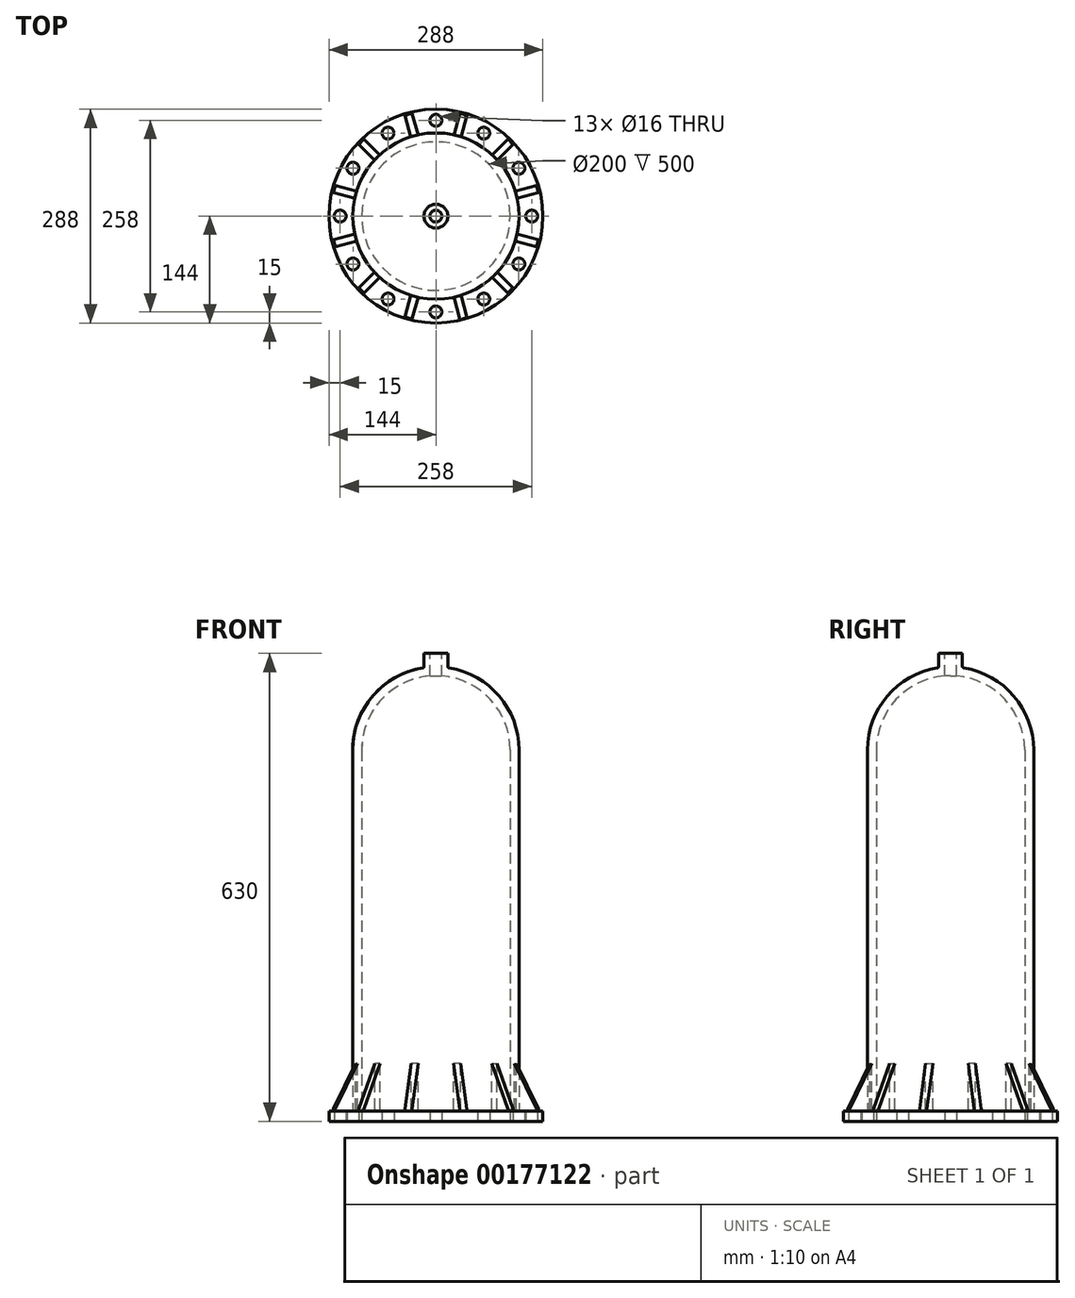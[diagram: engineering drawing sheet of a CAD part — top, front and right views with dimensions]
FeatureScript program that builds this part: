
annotation { "Feature Type Name" : "Feature", "Feature Type Description" : "" }
export const myFeature = defineFeature(function(context is Context, id is Id, definition is map)
    precondition{}
    {
        {
            var Q0;
            Q0=qCreatedBy(makeId("Front.planeOp"),FACE);
            var sketch = newSketch(context, id + "F0", { "sketchPlane" : qUnion([Q0])});
            skLineSegment(sketch, "E0", {"start": v(-144, 0) * mm, "end": v(-100, 0) * mm});
            skLineSegment(sketch, "E1", {"start": v(-100, 0) * mm, "end": v(-100, 500) * mm});
            skLineSegment(sketch, "E2", {"start": v(-144, 0) * mm, "end": v(-144, 14) * mm});
            skLineSegment(sketch, "E3", {"start": v(-16, 610.85) * mm, "end": v(-16, 630) * mm});
            skLineSegment(sketch, "E4", {"start": v(-16, 630) * mm, "end": v(0, 630) * mm});
            skLineSegment(sketch, "E5", {"start": v(0, 630) * mm, "end": v(0, 600) * mm});
            skLineSegment(sketch, "E6", {"start": v(0, 0) * mm, "end": v(0, 600) * mm, "construction": true});
            skPoint(sketch, "E7", {"position": v(0, 615) * mm});
            skLineSegment(sketch, "E8", {"start": v(-144, 14) * mm, "end": v(-112, 14) * mm});
            skLineSegment(sketch, "E9", {"start": v(-112, 14) * mm, "end": v(-112, 500) * mm});
            skArc(sketch, "E10", {"start": v(0, 600) * mm, "mid": v(-70.71, 570.71) * mm, "end": v(-100, 500) * mm});
            skArc(sketch, "E11", {"start": v(-16, 610.85) * mm, "mid": v(-84.66, 573.32) * mm, "end": v(-112, 500) * mm});
            skLineSegment(sketch, "E12", {"start": v(-112, 500) * mm, "end": v(0, 500) * mm, "construction": true});
            skSolve(sketch);
        }
        {
            var Q0;
            Q0 = qSketchRegion(id + "F0", true);
            var Q1;
            Q1=sQuery(id+"F0.wireOp",EDGE,"E6");
            revolve(context, id + "F1", {"entities" : qUnion([Q0]), "axis" : qUnion([Q1]), "revolveType" : RevolveType.FULL});
        }
        {
            var Q0;
            Q0=makeQuery(id+"F1.opRevolve","SWEPT_FACE",FACE,{"disambiguationData":[OSD([sQuery(id+"F0.wireOp",EDGE,"E0")])]});
            var sketch = newSketch(context, id + "F2", { "sketchPlane" : qUnion([Q0])});
            skCircle(sketch, "E13", {"center": v(0, -129) * mm, "radius": 8 * mm});
            skSolve(sketch);
        }
        {
            var Q0;
            Q0=makeQuery(id+"F2.imprint","IMPRINT",FACE,{"disambiguationData":[TD([[makeQuery(id+"F2.imprint","IMPRINT",EDGE,{"derivedFrom":sQuery(id+"F2.wireOp",EDGE,"E13")}),1.0]])]});
            extrude(context, id + "F3", {"entities" : qUnion([Q0]), "oppositeDirection" : true, "depth" : 20 * mm});
        }
        {
            var Q0;
            Q0=makeQuery(id+"F3.opExtrude","SWEPT_BODY",BODY,{"disambiguationData":[OSD([sQuery(id+"F2.wireOp",EDGE,"E13")])]});
            var Q1;
            Q1=makeQuery(id+"F1.opRevolve","SWEPT_EDGE",EDGE,{"disambiguationData":[OSD([sQuery(id+"F0.wireOp",EDGE,"E0"),sQuery(id+"F0.wireOp",EDGE,"E2")])]});
            circularPattern(context, id + "F4", {"entities" : qUnion([Q0]), "axis" : qUnion([Q1]), "angle" : 30 * degree, "instanceCount" : 12});
        }
        {
            var Q0;
            Q0=makeQuery(id+"F3.opExtrude","SWEPT_BODY",BODY,{"disambiguationData":[OSD([sQuery(id+"F2.wireOp",EDGE,"E13")])]});
            var Q1;
            Q1=makeQuery(id+"F4.opPattern","COPY",BODY,{"derivedFrom":makeQuery(id+"F3.opExtrude","SWEPT_BODY",BODY,{"disambiguationData":[OSD([sQuery(id+"F2.wireOp",EDGE,"E13")])]}),"instanceName":"2"});
            var Q2;
            Q2=makeQuery(id+"F4.opPattern","COPY",BODY,{"derivedFrom":makeQuery(id+"F3.opExtrude","SWEPT_BODY",BODY,{"disambiguationData":[OSD([sQuery(id+"F2.wireOp",EDGE,"E13")])]}),"instanceName":"4"});
            var Q3;
            Q3=makeQuery(id+"F4.opPattern","COPY",BODY,{"derivedFrom":makeQuery(id+"F3.opExtrude","SWEPT_BODY",BODY,{"disambiguationData":[OSD([sQuery(id+"F2.wireOp",EDGE,"E13")])]}),"instanceName":"6"});
            var Q4;
            Q4=makeQuery(id+"F4.opPattern","COPY",BODY,{"derivedFrom":makeQuery(id+"F3.opExtrude","SWEPT_BODY",BODY,{"disambiguationData":[OSD([sQuery(id+"F2.wireOp",EDGE,"E13")])]}),"instanceName":"8"});
            var Q5;
            Q5=makeQuery(id+"F4.opPattern","COPY",BODY,{"derivedFrom":makeQuery(id+"F3.opExtrude","SWEPT_BODY",BODY,{"disambiguationData":[OSD([sQuery(id+"F2.wireOp",EDGE,"E13")])]}),"instanceName":"11"});
            var Q6;
            Q6=makeQuery(id+"F4.opPattern","COPY",BODY,{"derivedFrom":makeQuery(id+"F3.opExtrude","SWEPT_BODY",BODY,{"disambiguationData":[OSD([sQuery(id+"F2.wireOp",EDGE,"E13")])]}),"instanceName":"10"});
            var Q7;
            Q7=makeQuery(id+"F4.opPattern","COPY",BODY,{"derivedFrom":makeQuery(id+"F3.opExtrude","SWEPT_BODY",BODY,{"disambiguationData":[OSD([sQuery(id+"F2.wireOp",EDGE,"E13")])]}),"instanceName":"9"});
            var Q8;
            Q8=makeQuery(id+"F4.opPattern","COPY",BODY,{"derivedFrom":makeQuery(id+"F3.opExtrude","SWEPT_BODY",BODY,{"disambiguationData":[OSD([sQuery(id+"F2.wireOp",EDGE,"E13")])]}),"instanceName":"7"});
            var Q9;
            Q9=makeQuery(id+"F4.opPattern","COPY",BODY,{"derivedFrom":makeQuery(id+"F3.opExtrude","SWEPT_BODY",BODY,{"disambiguationData":[OSD([sQuery(id+"F2.wireOp",EDGE,"E13")])]}),"instanceName":"5"});
            var Q10;
            Q10=makeQuery(id+"F4.opPattern","COPY",BODY,{"derivedFrom":makeQuery(id+"F3.opExtrude","SWEPT_BODY",BODY,{"disambiguationData":[OSD([sQuery(id+"F2.wireOp",EDGE,"E13")])]}),"instanceName":"3"});
            var Q11;
            Q11=makeQuery(id+"F4.opPattern","COPY",BODY,{"derivedFrom":makeQuery(id+"F3.opExtrude","SWEPT_BODY",BODY,{"disambiguationData":[OSD([sQuery(id+"F2.wireOp",EDGE,"E13")])]}),"instanceName":"1"});
            var Q12;
            Q12=makeQuery(id+"F1.opRevolve","SWEPT_BODY",BODY,{"disambiguationData":[OSD([sQuery(id+"F0.wireOp",EDGE,"E0"),sQuery(id+"F0.wireOp",EDGE,"E1"),sQuery(id+"F0.wireOp",EDGE,"E2"),sQuery(id+"F0.wireOp",EDGE,"E3"),sQuery(id+"F0.wireOp",EDGE,"E4"),sQuery(id+"F0.wireOp",EDGE,"E5"),sQuery(id+"F0.wireOp",EDGE,"E8"),sQuery(id+"F0.wireOp",EDGE,"E9"),sQuery(id+"F0.wireOp",EDGE,"E10"),sQuery(id+"F0.wireOp",EDGE,"E11")])]});
            booleanBodies(context, id + "F5", {"operationType" : BooleanOperationType.SUBTRACTION, "tools" : qUnion([Q0, Q1, Q2, Q3, Q4, Q5, Q6, Q7, Q8, Q9, Q10, Q11]), "targets" : qUnion([Q12])});
        }
        {
            var Q0;
            Q0=sQuery(id+"F0.wireOp",EDGE,"E6");
            cPlane(context, id + "F6", {"entities" : qUnion([Q0]), "cplaneType" : CPlaneType.LINE_ANGLE, "offset" : 25 * mm, "angle" : 45 * degree, "width" : 150 * mm, "height" : 150 * mm});
        }
        {
            var Q0;
            Q0=qCreatedBy(id+"F6.planeOp",FACE);
            var sketch = newSketch(context, id + "F7", { "sketchPlane" : qUnion([Q0])});
            skLineSegment(sketch, "E14", {"start": v(-111, 78) * mm, "end": v(-143, 14) * mm});
            skLineSegment(sketch, "E15", {"start": v(-143, 14) * mm, "end": v(-111, 14) * mm});
            skLineSegment(sketch, "E16", {"start": v(-111, 14) * mm, "end": v(-111, 78) * mm});
            skSolve(sketch);
        }
        {
            var Q0;
            Q0=makeQuery(id+"F7.imprint","IMPRINT",FACE,{"disambiguationData":[TD([[makeQuery(id+"F7.imprint","IMPRINT",EDGE,{"derivedFrom":sQuery(id+"F7.wireOp",EDGE,"E14")}),1.0]])]});
            extrude(context, id + "F8", {"entities" : qUnion([Q0]), "endBound" : BoundingType.SYMMETRIC, "depth" : 10 * mm});
        }
        {
            var Q0;
            Q0=makeQuery(id+"F8.opExtrude","SWEPT_BODY",BODY,{"disambiguationData":[OSD([sQuery(id+"F7.wireOp",EDGE,"E14"),sQuery(id+"F7.wireOp",EDGE,"E15"),sQuery(id+"F7.wireOp",EDGE,"E16")])]});
            var Q1;
            Q1=makeQuery(id+"F1.opRevolve","SWEPT_EDGE",EDGE,{"disambiguationData":[OSD([sQuery(id+"F0.wireOp",EDGE,"E0"),sQuery(id+"F0.wireOp",EDGE,"E2")])]});
            circularPattern(context, id + "F9", {"entities" : qUnion([Q0]), "axis" : qUnion([Q1]), "angle" : 30 * degree, "instanceCount" : 12});
        }
        {
            var Q0;
            Q0=makeQuery(id+"F1.opRevolve","SWEPT_FACE",FACE,{"disambiguationData":[OSD([sQuery(id+"F0.wireOp",EDGE,"E4")])]});
            var sketch = newSketch(context, id + "F10", { "sketchPlane" : qUnion([Q0])});
            skCircle(sketch, "E17", {"center": v(0, 0) * mm, "radius": 8 * mm});
            skSolve(sketch);
        }
        {
            var Q0;
            Q0=makeQuery(id+"F10.imprint","IMPRINT",FACE,{"disambiguationData":[TD([[makeQuery(id+"F10.imprint","IMPRINT",EDGE,{"derivedFrom":sQuery(id+"F10.wireOp",EDGE,"E17")}),1.0]])]});
            extrude(context, id + "F11", {"entities" : qUnion([Q0]), "operationType" : NewBodyOperationType.REMOVE, "endBound" : BoundingType.THROUGH_ALL, "oppositeDirection" : true, "depth" : 25 * mm});
        }
        {
            var Q0;
            Q0=makeQuery(id+"F1.opRevolve","SWEPT_EDGE",EDGE,{"disambiguationData":[OSD([sQuery(id+"F0.wireOp",EDGE,"E3"),sQuery(id+"F0.wireOp",EDGE,"E11")])]});
            fillet(context, id + "F12", {"entities" : qUnion([Q0]), "radius" : 2 * mm, "tangentPropagation" : true, "allowEdgeOverflow" : false});
        }
        {
            var Q0;
            Q0=makeQuery(id+"F1.opRevolve","SWEPT_FACE",FACE,{"disambiguationData":[OSD([sQuery(id+"F0.wireOp",EDGE,"E9")])]});
            fillet(context, id + "F13", {"entities" : qUnion([Q0]), "radius" : 2 * mm, "tangentPropagation" : true, "allowEdgeOverflow" : false});
        }
        {
            var Q0;
            Q0=makeQuery(id+"F9.opPattern","COPY",EDGE,{"derivedFrom":makeQuery(id+"F8.opExtrude","CAP_EDGE",EDGE,{"disambiguationData":[OSD([sQuery(id+"F7.wireOp",EDGE,"E15")])],"isStart":true}),"instanceName":"2"});
            var Q1;
            Q1=makeQuery(id+"F9.opPattern","COPY",EDGE,{"derivedFrom":makeQuery(id+"F8.opExtrude","CAP_EDGE",EDGE,{"disambiguationData":[OSD([sQuery(id+"F7.wireOp",EDGE,"E15")])],"isStart":false}),"instanceName":"2"});
            var Q2;
            Q2=makeQuery(id+"F9.opPattern","COPY",EDGE,{"derivedFrom":makeQuery(id+"F8.opExtrude","CAP_EDGE",EDGE,{"disambiguationData":[OSD([sQuery(id+"F7.wireOp",EDGE,"E15")])],"isStart":false}),"instanceName":"3"});
            var Q3;
            Q3=makeQuery(id+"F9.opPattern","COPY",EDGE,{"derivedFrom":makeQuery(id+"F8.opExtrude","SWEPT_EDGE",EDGE,{"disambiguationData":[OSD([sQuery(id+"F7.wireOp",EDGE,"E14"),sQuery(id+"F7.wireOp",EDGE,"E15")])]}),"instanceName":"2"});
            var Q4;
            Q4=makeQuery(id+"F9.opPattern","COPY",EDGE,{"derivedFrom":makeQuery(id+"F8.opExtrude","SWEPT_EDGE",EDGE,{"disambiguationData":[OSD([sQuery(id+"F7.wireOp",EDGE,"E14"),sQuery(id+"F7.wireOp",EDGE,"E15")])]}),"instanceName":"3"});
            var Q5;
            Q5=makeQuery(id+"F9.opPattern","COPY",EDGE,{"derivedFrom":makeQuery(id+"F8.opExtrude","CAP_EDGE",EDGE,{"disambiguationData":[OSD([sQuery(id+"F7.wireOp",EDGE,"E15")])],"isStart":true}),"instanceName":"3"});
            var Q6;
            Q6=makeQuery(id+"F9.opPattern","COPY",EDGE,{"derivedFrom":makeQuery(id+"F8.opExtrude","CAP_EDGE",EDGE,{"disambiguationData":[OSD([sQuery(id+"F7.wireOp",EDGE,"E15")])],"isStart":false}),"instanceName":"4"});
            var Q7;
            Q7=makeQuery(id+"F9.opPattern","COPY",EDGE,{"derivedFrom":makeQuery(id+"F8.opExtrude","SWEPT_EDGE",EDGE,{"disambiguationData":[OSD([sQuery(id+"F7.wireOp",EDGE,"E14"),sQuery(id+"F7.wireOp",EDGE,"E15")])]}),"instanceName":"4"});
            var Q8;
            Q8=makeQuery(id+"F9.opPattern","COPY",EDGE,{"derivedFrom":makeQuery(id+"F8.opExtrude","CAP_EDGE",EDGE,{"disambiguationData":[OSD([sQuery(id+"F7.wireOp",EDGE,"E15")])],"isStart":true}),"instanceName":"4"});
            var Q9;
            Q9=makeQuery(id+"F9.opPattern","COPY",EDGE,{"derivedFrom":makeQuery(id+"F8.opExtrude","CAP_EDGE",EDGE,{"disambiguationData":[OSD([sQuery(id+"F7.wireOp",EDGE,"E15")])],"isStart":false}),"instanceName":"5"});
            var Q10;
            Q10=makeQuery(id+"F9.opPattern","COPY",EDGE,{"derivedFrom":makeQuery(id+"F8.opExtrude","SWEPT_EDGE",EDGE,{"disambiguationData":[OSD([sQuery(id+"F7.wireOp",EDGE,"E14"),sQuery(id+"F7.wireOp",EDGE,"E15")])]}),"instanceName":"5"});
            var Q11;
            Q11=makeQuery(id+"F9.opPattern","COPY",EDGE,{"derivedFrom":makeQuery(id+"F8.opExtrude","CAP_EDGE",EDGE,{"disambiguationData":[OSD([sQuery(id+"F7.wireOp",EDGE,"E15")])],"isStart":true}),"instanceName":"5"});
            var Q12;
            Q12=makeQuery(id+"F9.opPattern","COPY",EDGE,{"derivedFrom":makeQuery(id+"F8.opExtrude","CAP_EDGE",EDGE,{"disambiguationData":[OSD([sQuery(id+"F7.wireOp",EDGE,"E15")])],"isStart":false}),"instanceName":"6"});
            var Q13;
            Q13=makeQuery(id+"F9.opPattern","COPY",EDGE,{"derivedFrom":makeQuery(id+"F8.opExtrude","SWEPT_EDGE",EDGE,{"disambiguationData":[OSD([sQuery(id+"F7.wireOp",EDGE,"E14"),sQuery(id+"F7.wireOp",EDGE,"E15")])]}),"instanceName":"6"});
            var Q14;
            Q14=makeQuery(id+"F9.opPattern","COPY",EDGE,{"derivedFrom":makeQuery(id+"F8.opExtrude","CAP_EDGE",EDGE,{"disambiguationData":[OSD([sQuery(id+"F7.wireOp",EDGE,"E15")])],"isStart":true}),"instanceName":"6"});
            var Q15;
            Q15=makeQuery(id+"F9.opPattern","COPY",EDGE,{"derivedFrom":makeQuery(id+"F8.opExtrude","CAP_EDGE",EDGE,{"disambiguationData":[OSD([sQuery(id+"F7.wireOp",EDGE,"E15")])],"isStart":false}),"instanceName":"7"});
            var Q16;
            Q16=makeQuery(id+"F9.opPattern","COPY",EDGE,{"derivedFrom":makeQuery(id+"F8.opExtrude","SWEPT_EDGE",EDGE,{"disambiguationData":[OSD([sQuery(id+"F7.wireOp",EDGE,"E14"),sQuery(id+"F7.wireOp",EDGE,"E15")])]}),"instanceName":"7"});
            var Q17;
            Q17=makeQuery(id+"F9.opPattern","COPY",EDGE,{"derivedFrom":makeQuery(id+"F8.opExtrude","CAP_EDGE",EDGE,{"disambiguationData":[OSD([sQuery(id+"F7.wireOp",EDGE,"E15")])],"isStart":true}),"instanceName":"7"});
            var Q18;
            Q18=makeQuery(id+"F9.opPattern","COPY",EDGE,{"derivedFrom":makeQuery(id+"F8.opExtrude","CAP_EDGE",EDGE,{"disambiguationData":[OSD([sQuery(id+"F7.wireOp",EDGE,"E15")])],"isStart":false}),"instanceName":"8"});
            var Q19;
            Q19=makeQuery(id+"F9.opPattern","COPY",EDGE,{"derivedFrom":makeQuery(id+"F8.opExtrude","SWEPT_EDGE",EDGE,{"disambiguationData":[OSD([sQuery(id+"F7.wireOp",EDGE,"E14"),sQuery(id+"F7.wireOp",EDGE,"E15")])]}),"instanceName":"8"});
            var Q20;
            Q20=makeQuery(id+"F9.opPattern","COPY",EDGE,{"derivedFrom":makeQuery(id+"F8.opExtrude","CAP_EDGE",EDGE,{"disambiguationData":[OSD([sQuery(id+"F7.wireOp",EDGE,"E15")])],"isStart":true}),"instanceName":"8"});
            var Q21;
            Q21=makeQuery(id+"F9.opPattern","COPY",EDGE,{"derivedFrom":makeQuery(id+"F8.opExtrude","CAP_EDGE",EDGE,{"disambiguationData":[OSD([sQuery(id+"F7.wireOp",EDGE,"E15")])],"isStart":false}),"instanceName":"9"});
            var Q22;
            Q22=makeQuery(id+"F9.opPattern","COPY",EDGE,{"derivedFrom":makeQuery(id+"F8.opExtrude","SWEPT_EDGE",EDGE,{"disambiguationData":[OSD([sQuery(id+"F7.wireOp",EDGE,"E14"),sQuery(id+"F7.wireOp",EDGE,"E15")])]}),"instanceName":"9"});
            var Q23;
            Q23=makeQuery(id+"F9.opPattern","COPY",EDGE,{"derivedFrom":makeQuery(id+"F8.opExtrude","CAP_EDGE",EDGE,{"disambiguationData":[OSD([sQuery(id+"F7.wireOp",EDGE,"E15")])],"isStart":true}),"instanceName":"9"});
            var Q24;
            Q24=makeQuery(id+"F9.opPattern","COPY",EDGE,{"derivedFrom":makeQuery(id+"F8.opExtrude","CAP_EDGE",EDGE,{"disambiguationData":[OSD([sQuery(id+"F7.wireOp",EDGE,"E15")])],"isStart":false}),"instanceName":"10"});
            var Q25;
            Q25=makeQuery(id+"F9.opPattern","COPY",EDGE,{"derivedFrom":makeQuery(id+"F8.opExtrude","SWEPT_EDGE",EDGE,{"disambiguationData":[OSD([sQuery(id+"F7.wireOp",EDGE,"E14"),sQuery(id+"F7.wireOp",EDGE,"E15")])]}),"instanceName":"10"});
            var Q26;
            Q26=makeQuery(id+"F9.opPattern","COPY",EDGE,{"derivedFrom":makeQuery(id+"F8.opExtrude","CAP_EDGE",EDGE,{"disambiguationData":[OSD([sQuery(id+"F7.wireOp",EDGE,"E15")])],"isStart":true}),"instanceName":"10"});
            var Q27;
            Q27=makeQuery(id+"F9.opPattern","COPY",EDGE,{"derivedFrom":makeQuery(id+"F8.opExtrude","CAP_EDGE",EDGE,{"disambiguationData":[OSD([sQuery(id+"F7.wireOp",EDGE,"E15")])],"isStart":false}),"instanceName":"11"});
            var Q28;
            Q28=makeQuery(id+"F9.opPattern","COPY",EDGE,{"derivedFrom":makeQuery(id+"F8.opExtrude","SWEPT_EDGE",EDGE,{"disambiguationData":[OSD([sQuery(id+"F7.wireOp",EDGE,"E14"),sQuery(id+"F7.wireOp",EDGE,"E15")])]}),"instanceName":"11"});
            var Q29;
            Q29=makeQuery(id+"F9.opPattern","COPY",EDGE,{"derivedFrom":makeQuery(id+"F8.opExtrude","CAP_EDGE",EDGE,{"disambiguationData":[OSD([sQuery(id+"F7.wireOp",EDGE,"E15")])],"isStart":true}),"instanceName":"11"});
            var Q30;
            Q30=makeQuery(id+"F8.opExtrude","CAP_EDGE",EDGE,{"disambiguationData":[OSD([sQuery(id+"F7.wireOp",EDGE,"E15")])],"isStart":false});
            var Q31;
            Q31=makeQuery(id+"F8.opExtrude","SWEPT_EDGE",EDGE,{"disambiguationData":[OSD([sQuery(id+"F7.wireOp",EDGE,"E14"),sQuery(id+"F7.wireOp",EDGE,"E15")])]});
            var Q32;
            Q32=makeQuery(id+"F8.opExtrude","CAP_EDGE",EDGE,{"disambiguationData":[OSD([sQuery(id+"F7.wireOp",EDGE,"E15")])],"isStart":true});
            var Q33;
            Q33=makeQuery(id+"F9.opPattern","COPY",EDGE,{"derivedFrom":makeQuery(id+"F8.opExtrude","CAP_EDGE",EDGE,{"disambiguationData":[OSD([sQuery(id+"F7.wireOp",EDGE,"E15")])],"isStart":false}),"instanceName":"1"});
            var Q34;
            Q34=makeQuery(id+"F9.opPattern","COPY",EDGE,{"derivedFrom":makeQuery(id+"F8.opExtrude","CAP_EDGE",EDGE,{"disambiguationData":[OSD([sQuery(id+"F7.wireOp",EDGE,"E15")])],"isStart":true}),"instanceName":"1"});
            fillet(context, id + "F14", {"entities" : qUnion([Q0, Q1, Q2, Q3, Q4, Q5, Q6, Q7, Q8, Q9, Q10, Q11, Q12, Q13, Q14, Q15, Q16, Q17, Q18, Q19, Q20, Q21, Q22, Q23, Q24, Q25, Q26, Q27, Q28, Q29, Q30, Q31, Q32, Q33, Q34]), "radius" : 2 * mm, "tangentPropagation" : true, "allowEdgeOverflow" : false});
        }
    });
